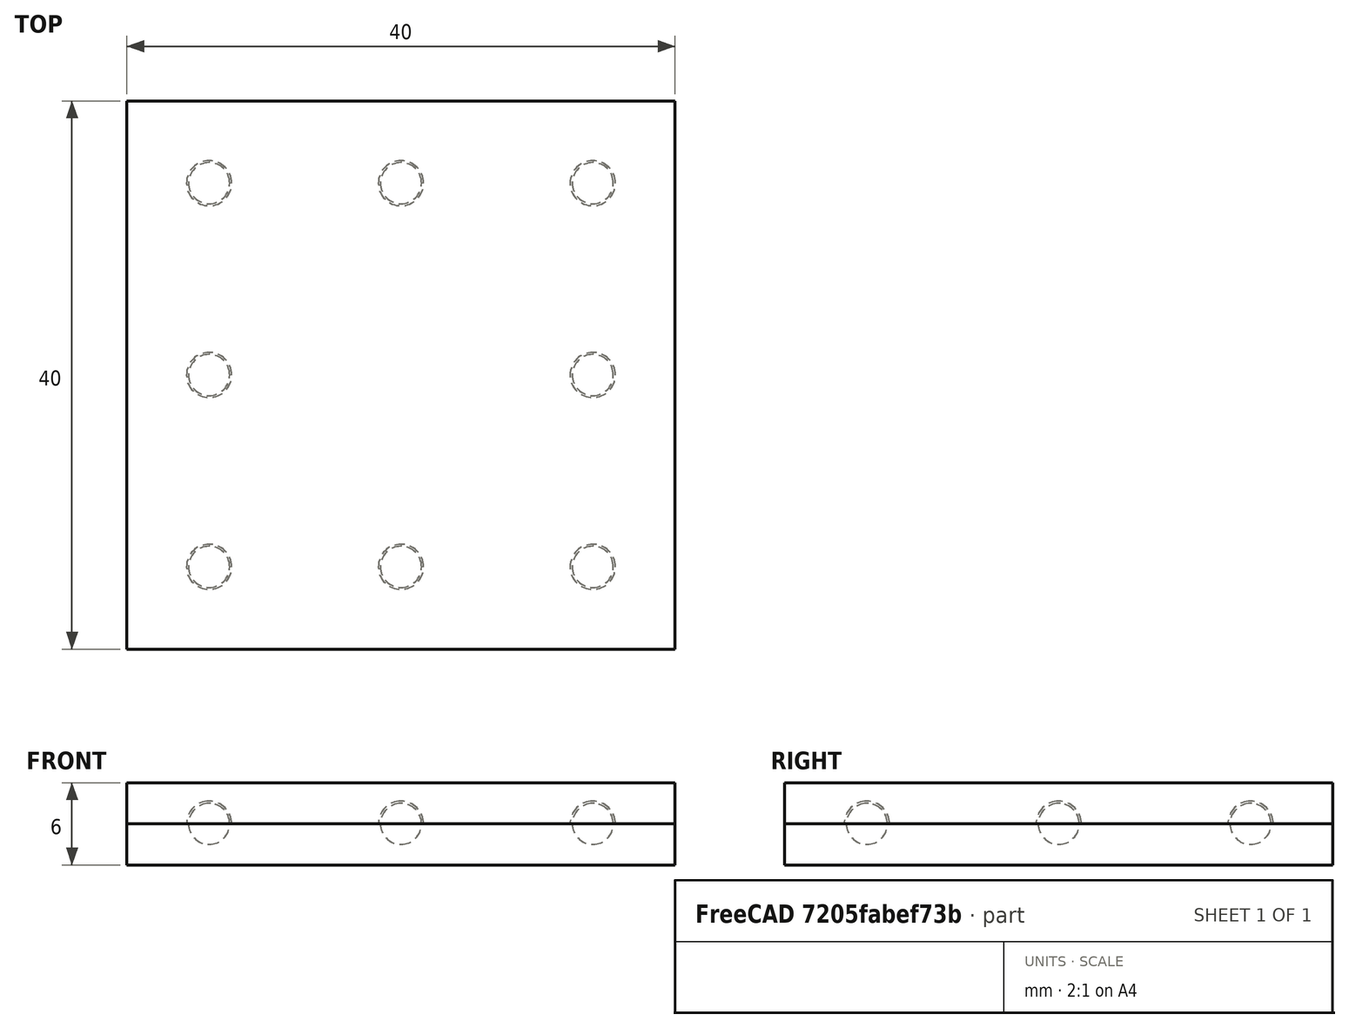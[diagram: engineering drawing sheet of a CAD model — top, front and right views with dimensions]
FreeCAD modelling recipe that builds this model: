
FCSTD DOCUMENT  (FreeCAD 0.17R13522 (Git))
Label: Bumps and Dips
License: All rights reserved
LicenseURL: http://en.wikipedia.org/wiki/All_rights_reserved
objects: Part::Sphere×16, Part::MultiFuse×3, Part::Box×2, Part::Cut×1, Part::Fuse×1
note: 23 computed .brp shape members not serialized (recipe doc carries the construction recipe); baked Part::Feature solids carry a one-line shape summary decoded from their .brp

FEATURE [Part::Box] Box  label="Cube"
  AttacherType = Attacher::AttachEngine3D
  Height = 3
  Length = 40
  Width = 40
FEATURE [Part::Box] Box001  label="Cube001"
  AttacherType = Attacher::AttachEngine3D
  Height = 3
  Length = 40
  Placement = pos=(0,0,3) rot=(0,0,1;0rad)
  Width = 40
FEATURE [Part::Sphere] Sphere
  Angle1 = -90
  Angle2 = 90
  Angle3 = 360
  AttacherType = Attacher::AttachEngine3D
  Placement = pos=(6,6,3) rot=(0,0,1;0rad)
  Radius = 1.5
FEATURE [Part::Sphere] Sphere001
  Angle1 = -90
  Angle2 = 90
  Angle3 = 360
  AttacherType = Attacher::AttachEngine3D
  Placement = pos=(34,6,3) rot=(0,0,1;0rad)
  Radius = 1.5
FEATURE [Part::Sphere] Sphere002
  Angle1 = -90
  Angle2 = 90
  Angle3 = 360
  AttacherType = Attacher::AttachEngine3D
  Placement = pos=(34,34,3) rot=(0,0,1;0rad)
  Radius = 1.5
FEATURE [Part::Sphere] Sphere003
  Angle1 = -90
  Angle2 = 90
  Angle3 = 360
  AttacherType = Attacher::AttachEngine3D
  Placement = pos=(6,34,3) rot=(0,0,1;0rad)
  Radius = 1.5
FEATURE [Part::Sphere] Sphere004
  Angle1 = -90
  Angle2 = 90
  Angle3 = 360
  AttacherType = Attacher::AttachEngine3D
  Placement = pos=(6,20,3) rot=(0,0,1;0rad)
  Radius = 1.5
FEATURE [Part::Sphere] Sphere005
  Angle1 = -90
  Angle2 = 90
  Angle3 = 360
  AttacherType = Attacher::AttachEngine3D
  Placement = pos=(34,20,3) rot=(0,0,1;0rad)
  Radius = 1.5
FEATURE [Part::Sphere] Sphere006
  Angle1 = -90
  Angle2 = 90
  Angle3 = 360
  AttacherType = Attacher::AttachEngine3D
  Placement = pos=(20,6,3) rot=(0,0,1;0rad)
  Radius = 1.5
FEATURE [Part::Sphere] Sphere007
  Angle1 = -90
  Angle2 = 90
  Angle3 = 360
  AttacherType = Attacher::AttachEngine3D
  Placement = pos=(20,34,3) rot=(0,0,1;0rad)
  Radius = 1.5
FEATURE [Part::Sphere] Sphere008
  Angle1 = -90
  Angle2 = 90
  Angle3 = 360
  AttacherType = Attacher::AttachEngine3D
  Placement = pos=(6,6,3) rot=(0,0,1;0rad)
  Radius = 1.65
FEATURE [Part::Sphere] Sphere009
  Angle1 = -90
  Angle2 = 90
  Angle3 = 360
  AttacherType = Attacher::AttachEngine3D
  Placement = pos=(34,20,3) rot=(0,0,1;0rad)
  Radius = 1.65
FEATURE [Part::Sphere] Sphere010
  Angle1 = -90
  Angle2 = 90
  Angle3 = 360
  AttacherType = Attacher::AttachEngine3D
  Placement = pos=(34,6,3) rot=(0,0,1;0rad)
  Radius = 1.65
FEATURE [Part::Sphere] Sphere011
  Angle1 = -90
  Angle2 = 90
  Angle3 = 360
  AttacherType = Attacher::AttachEngine3D
  Placement = pos=(20,34,3) rot=(0,0,1;0rad)
  Radius = 1.65
FEATURE [Part::Sphere] Sphere012
  Angle1 = -90
  Angle2 = 90
  Angle3 = 360
  AttacherType = Attacher::AttachEngine3D
  Placement = pos=(20,6,3) rot=(0,0,1;0rad)
  Radius = 1.65
FEATURE [Part::Sphere] Sphere013
  Angle1 = -90
  Angle2 = 90
  Angle3 = 360
  AttacherType = Attacher::AttachEngine3D
  Placement = pos=(6,34,3) rot=(0,0,1;0rad)
  Radius = 1.65
FEATURE [Part::Sphere] Sphere014
  Angle1 = -90
  Angle2 = 90
  Angle3 = 360
  AttacherType = Attacher::AttachEngine3D
  Placement = pos=(34,34,3) rot=(0,0,1;0rad)
  Radius = 1.65
FEATURE [Part::Sphere] Sphere015
  Angle1 = -90
  Angle2 = 90
  Angle3 = 360
  AttacherType = Attacher::AttachEngine3D
  Placement = pos=(6,20,3) rot=(0,0,1;0rad)
  Radius = 1.65
FEATURE [Part::MultiFuse] Fusion001
  Shapes = -> [Sphere008,Sphere009,Sphere010,Sphere011,Sphere012,Sphere013,Sphere014,Sphere015]
FEATURE [Part::Cut] Cut  label="Dips"
  Base = -> Box001
  Tool = -> Fusion001
FEATURE [Part::MultiFuse] Fusion
  Shapes = -> [Sphere,Sphere005,Sphere003]
FEATURE [Part::MultiFuse] Fusion002  label="Spare bumps"
  Shapes = -> [Sphere001,Sphere007,Sphere002,Sphere004,Sphere006]
FEATURE [Part::Fuse] Fusion003
  Base = -> Box
  Tool = -> Fusion
